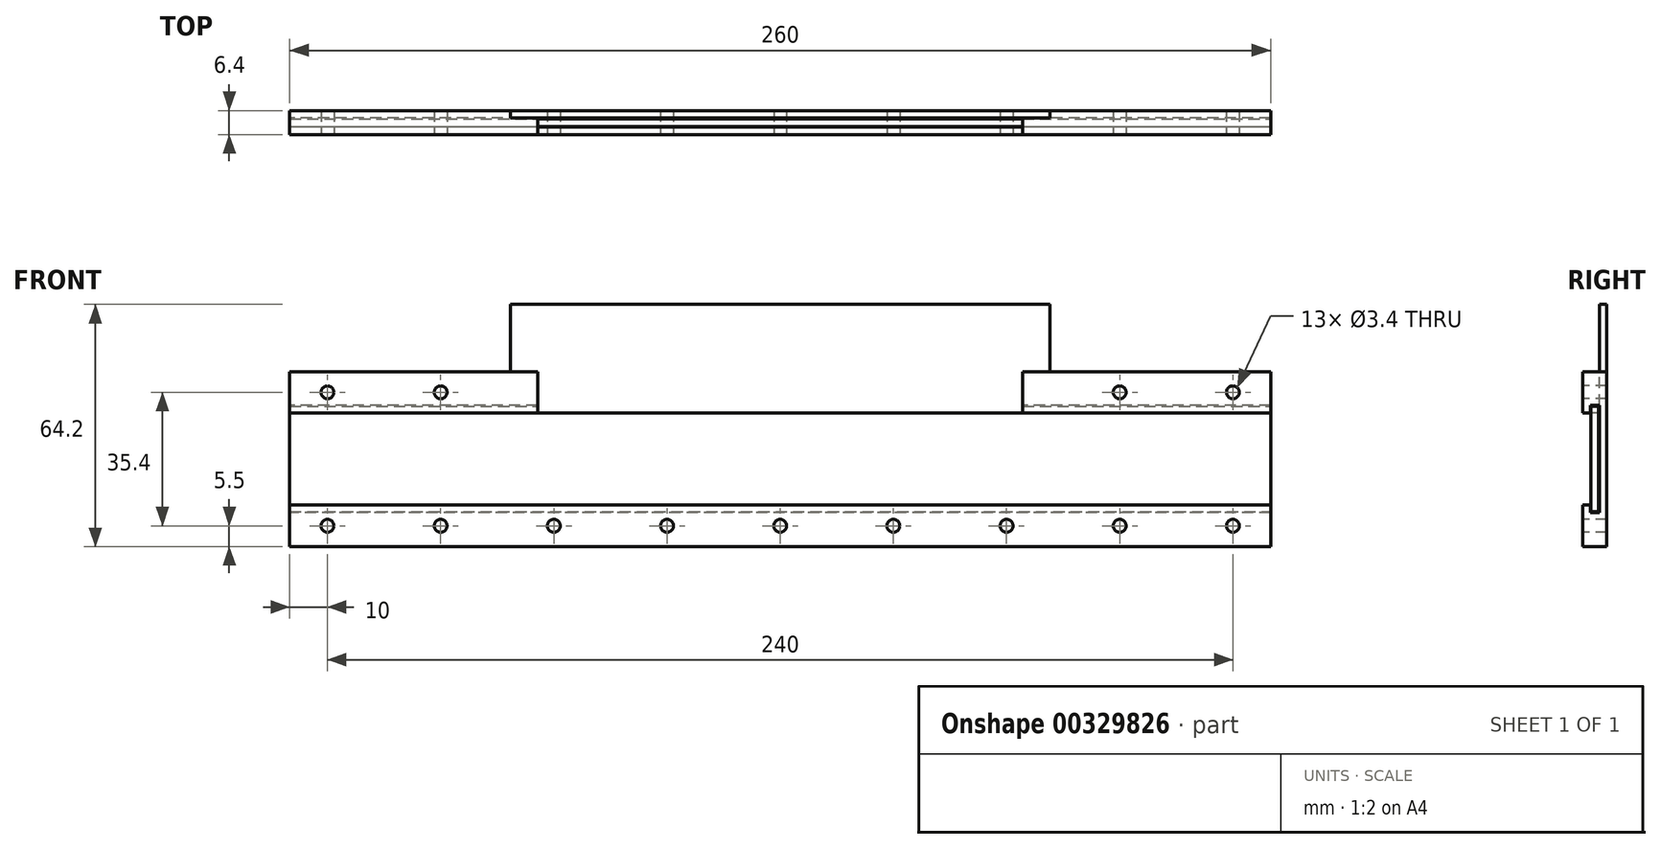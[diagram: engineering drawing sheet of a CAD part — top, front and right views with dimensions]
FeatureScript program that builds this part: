
annotation { "Feature Type Name" : "Feature", "Feature Type Description" : "" }
export const myFeature = defineFeature(function(context is Context, id is Id, definition is map)
    precondition{}
    {
        {
            var Q0;
            Q0=qCreatedBy(makeId("Front.planeOp"),FACE);
            var sketch = newSketch(context, id + "F0", { "sketchPlane" : qUnion([Q0])});
            skLineSegment(sketch, "E0.bottom", {"start": v(-130, 28) * mm, "end": v(130, 28) * mm});
            skLineSegment(sketch, "E0.top", {"start": v(-130, 0) * mm, "end": v(130, 0) * mm});
            skLineSegment(sketch, "E0.left", {"start": v(-130, 28) * mm, "end": v(-130, 0) * mm});
            skLineSegment(sketch, "E0.right", {"start": v(130, 28) * mm, "end": v(130, 0) * mm});
            skSolve(sketch);
        }
        {
            var Q0;
            Q0=makeQuery(id+"F0.imprint","IMPRINT",FACE,{"disambiguationData":[TD([[makeQuery(id+"F0.imprint","IMPRINT",EDGE,{"derivedFrom":sQuery(id+"F0.wireOp",EDGE,"E0.bottom")}),-1.0]])]});
            extrude(context, id + "F1", {"entities" : qUnion([Q0]), "depth" : 2 * mm});
        }
        {
            var Q0;
            Q0=qCreatedBy(makeId("Front.planeOp"),FACE);
            var sketch = newSketch(context, id + "F2", { "sketchPlane" : qUnion([Q0])});
            skLineSegment(sketch, "E1.bottom", {"start": v(-62.5, 46) * mm, "end": v(62.5, 46) * mm});
            skLineSegment(sketch, "E1.top", {"start": v(-62.5, 28) * mm, "end": v(62.5, 28) * mm});
            skLineSegment(sketch, "E1.left", {"start": v(-62.5, 46) * mm, "end": v(-62.5, 28) * mm});
            skLineSegment(sketch, "E1.right", {"start": v(62.5, 46) * mm, "end": v(62.5, 28) * mm});
            skSolve(sketch);
        }
        {
            var Q0;
            Q0=makeQuery(id+"F2.imprint","IMPRINT",FACE,{"disambiguationData":[TD([[makeQuery(id+"F2.imprint","IMPRINT",EDGE,{"derivedFrom":sQuery(id+"F2.wireOp",EDGE,"E1.bottom")}),-1.0]])]});
            extrude(context, id + "F3", {"entities" : qUnion([Q0]), "depth" : 1 * mm});
        }
        {
            var Q0;
            Q0=qCreatedBy(makeId("Right.planeOp"),FACE);
            var sketch = newSketch(context, id + "F4", { "sketchPlane" : qUnion([Q0])});
            skLineSegment(sketch, "E2", {"start": v(-2.2, 1.8) * mm, "end": v(-2.2, -0.2) * mm});
            skLineSegment(sketch, "E3", {"start": v(-2.2, -0.2) * mm, "end": v(0.2, -0.2) * mm});
            skLineSegment(sketch, "E4", {"start": v(0.2, -0.2) * mm, "end": v(0.2, 28.2) * mm});
            skLineSegment(sketch, "E5", {"start": v(0.2, 28.2) * mm, "end": v(-2.2, 28.2) * mm});
            skLineSegment(sketch, "E6", {"start": v(-2.2, 28.2) * mm, "end": v(-2.2, 26.2) * mm});
            skLineSegment(sketch, "E7", {"start": v(-2.2, 26.2) * mm, "end": v(-4.2, 26.2) * mm});
            skLineSegment(sketch, "E8", {"start": v(-4.2, 26.2) * mm, "end": v(-4.2, 37.2) * mm});
            skLineSegment(sketch, "E9", {"start": v(-4.2, 37.2) * mm, "end": v(2.2, 37.2) * mm});
            skLineSegment(sketch, "E10", {"start": v(2.2, 37.2) * mm, "end": v(2.2, -9.2) * mm});
            skLineSegment(sketch, "E11", {"start": v(2.2, -9.2) * mm, "end": v(-4.2, -9.2) * mm});
            skLineSegment(sketch, "E12", {"start": v(-4.2, -9.2) * mm, "end": v(-4.2, 1.8) * mm});
            skLineSegment(sketch, "E13", {"start": v(-4.2, 1.8) * mm, "end": v(-2.2, 1.8) * mm});
            skLineSegment(sketch, "E14", {"start": v(-2.2, 1.8) * mm, "end": v(-2, 1.8) * mm, "construction": true});
            skLineSegment(sketch, "E15", {"start": v(0.2, 1.8) * mm, "end": v(0, 1.8) * mm, "construction": true});
            skLineSegment(sketch, "E16", {"start": v(0, -0.2) * mm, "end": v(0, 0) * mm, "construction": true});
            skLineSegment(sketch, "E17", {"start": v(-2.2, 28) * mm, "end": v(-2, 28) * mm, "construction": true});
            skLineSegment(sketch, "E18", {"start": v(-2, 28) * mm, "end": v(-2, 28.2) * mm, "construction": true});
            skLineSegment(sketch, "E19", {"start": v(0.2, 28) * mm, "end": v(0, 28) * mm, "construction": true});
            skSolve(sketch);
        }
        {
            var Q0;
            Q0 = qSketchRegion(id + "F4", true);
            extrude(context, id + "F5", {"entities" : qUnion([Q0]), "depth" : 260 * mm, "symmetric" : true});
        }
        {
            var Q0;
            Q0=makeQuery(id+"F5.opExtrude","SWEPT_FACE",FACE,{"disambiguationData":[OSD([sQuery(id+"F4.wireOp",EDGE,"E12")])]});
            var sketch = newSketch(context, id + "F6", { "sketchPlane" : qUnion([Q0])});
            skCircle(sketch, "E20", {"center": v(-120, -3.7) * mm, "radius": 1.7 * mm});
            skCircle(sketch, "E21.0.1.0", {"center": v(-120, 31.7) * mm, "radius": 1.7 * mm});
            skCircle(sketch, "E21.1.0.0", {"center": v(-90, -3.7) * mm, "radius": 1.7 * mm});
            skCircle(sketch, "E21.1.1.0", {"center": v(-90, 31.7) * mm, "radius": 1.7 * mm});
            skCircle(sketch, "E21.2.0.0", {"center": v(-60, -3.7) * mm, "radius": 1.7 * mm});
            skCircle(sketch, "E21.2.1.0", {"center": v(-60, 31.7) * mm, "radius": 1.7 * mm});
            skCircle(sketch, "E21.3.0.0", {"center": v(-30, -3.7) * mm, "radius": 1.7 * mm});
            skCircle(sketch, "E21.3.1.0", {"center": v(-30, 31.7) * mm, "radius": 1.7 * mm});
            skCircle(sketch, "E21.4.0.0", {"center": v(0, -3.7) * mm, "radius": 1.7 * mm});
            skCircle(sketch, "E21.4.1.0", {"center": v(0, 31.7) * mm, "radius": 1.7 * mm});
            skCircle(sketch, "E21.5.0.0", {"center": v(30, -3.7) * mm, "radius": 1.7 * mm});
            skCircle(sketch, "E21.5.1.0", {"center": v(30, 31.7) * mm, "radius": 1.7 * mm});
            skCircle(sketch, "E21.6.0.0", {"center": v(60, -3.7) * mm, "radius": 1.7 * mm});
            skCircle(sketch, "E21.6.1.0", {"center": v(60, 31.7) * mm, "radius": 1.7 * mm});
            skCircle(sketch, "E21.7.0.0", {"center": v(90, -3.7) * mm, "radius": 1.7 * mm});
            skCircle(sketch, "E21.7.1.0", {"center": v(90, 31.7) * mm, "radius": 1.7 * mm});
            skCircle(sketch, "E21.8.0.0", {"center": v(120, -3.7) * mm, "radius": 1.7 * mm});
            skCircle(sketch, "E21.8.1.0", {"center": v(120, 31.7) * mm, "radius": 1.7 * mm});
            skLineSegment(sketch, "E21.direction1", {"start": v(-120, -3.7) * mm, "end": v(-90, -3.7) * mm, "construction": true});
            skLineSegment(sketch, "E21.direction2", {"start": v(-120, -3.7) * mm, "end": v(-120, 31.7) * mm, "construction": true});
            skLineSegment(sketch, "E22", {"start": v(120, -3.7) * mm, "end": v(120, 1.8) * mm, "construction": true});
            skLineSegment(sketch, "E23", {"start": v(120, -3.7) * mm, "end": v(120, -9.2) * mm, "construction": true});
            skLineSegment(sketch, "E24", {"start": v(120, 31.7) * mm, "end": v(120, 26.2) * mm});
            skLineSegment(sketch, "E25", {"start": v(120, 31.7) * mm, "end": v(120, 37.2) * mm});
            skSolve(sketch);
        }
        {
            var Q0;
            Q0 = qSketchRegion(id + "F6", true);
            extrude(context, id + "F7", {"entities" : qUnion([Q0]), "operationType" : NewBodyOperationType.REMOVE, "endBound" : BoundingType.THROUGH_ALL, "oppositeDirection" : true, "depth" : 25 * mm});
        }
        {
            var Q0;
            Q0=makeQuery(id+"F5.opExtrude","SWEPT_FACE",FACE,{"disambiguationData":[OSD([sQuery(id+"F4.wireOp",EDGE,"E8")])]});
            var sketch = newSketch(context, id + "F8", { "sketchPlane" : qUnion([Q0])});
            skLineSegment(sketch, "E26.0", {"start": v(-64.3, 47.8) * mm, "end": v(64.3, 47.8) * mm});
            skLineSegment(sketch, "E26.1", {"start": v(-64.3, 47.8) * mm, "end": v(-64.3, 26.2) * mm});
            skLineSegment(sketch, "E26.2", {"start": v(-64.3, 26.2) * mm, "end": v(64.3, 26.2) * mm});
            skLineSegment(sketch, "E26.3", {"start": v(64.3, 47.8) * mm, "end": v(64.3, 26.2) * mm});
            skSolve(sketch);
        }
        {
            var Q0;
            Q0 = qSketchRegion(id + "F8", true);
            extrude(context, id + "F9", {"entities" : qUnion([Q0]), "operationType" : NewBodyOperationType.REMOVE, "endBound" : BoundingType.THROUGH_ALL, "oppositeDirection" : true, "depth" : 25 * mm});
        }
        {
            var Q0;
            Q0=makeQuery(id+"F5.opExtrude","SWEPT_FACE",FACE,{"disambiguationData":[OSD([sQuery(id+"F4.wireOp",EDGE,"E4")])]});
            var sketch = newSketch(context, id + "F10", { "sketchPlane" : qUnion([Q0])});
            skLineSegment(sketch, "E27", {"start": v(-71.5, 37.2) * mm, "end": v(-71.5, 55) * mm});
            skLineSegment(sketch, "E28", {"start": v(-71.5, 55) * mm, "end": v(71.5, 55) * mm});
            skLineSegment(sketch, "E29", {"start": v(71.5, 55) * mm, "end": v(71.5, 37.2) * mm});
            skLineSegment(sketch, "E30", {"start": v(71.5, 37.2) * mm, "end": v(64.3, 37.2) * mm});
            skLineSegment(sketch, "E31", {"start": v(64.3, 37.2) * mm, "end": v(64.3, 26.2) * mm});
            skLineSegment(sketch, "E32", {"start": v(64.3, 26.2) * mm, "end": v(-64.3, 26.2) * mm});
            skLineSegment(sketch, "E33", {"start": v(-64.3, 26.2) * mm, "end": v(-64.3, 37.2) * mm});
            skLineSegment(sketch, "E34", {"start": v(-64.3, 37.2) * mm, "end": v(-71.5, 37.2) * mm});
            skLineSegment(sketch, "E35", {"start": v(-71.5, 46) * mm, "end": v(-62.5, 46) * mm, "construction": true});
            skLineSegment(sketch, "E36", {"start": v(-62.5, 46) * mm, "end": v(-62.5, 55) * mm, "construction": true});
            skSolve(sketch);
        }
        {
            var Q0;
            Q0 = qSketchRegion(id + "F10", true);
            var Q1;
            Q1=makeQuery(id+"F5.opExtrude","SWEPT_FACE",FACE,{"disambiguationData":[OSD([sQuery(id+"F4.wireOp",EDGE,"E10")])]});
            extrude(context, id + "F11", {"entities" : qUnion([Q0]), "operationType" : NewBodyOperationType.ADD, "endBound" : BoundingType.UP_TO_SURFACE, "oppositeDirection" : true, "endBoundEntityFace" : qUnion([Q1]), "depth" : 25 * mm});
        }
    });
